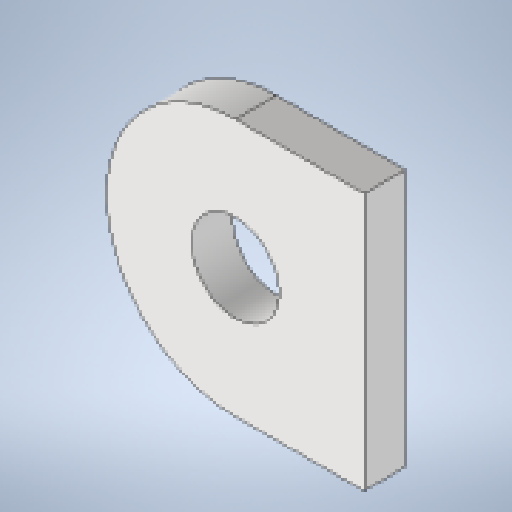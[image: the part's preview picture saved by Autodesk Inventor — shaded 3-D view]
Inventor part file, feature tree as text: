
AUTODESK INVENTOR PART (.ipt)
format: ipt  version: 2025.1 (Build 291241020, 241B)  size: 160,768 bytes
history: native  units: mm
features: other x2, sheet_metal_op x1, sketch x1
ambient origin geometry x8: Origin, YZ Plane, XZ Plane, XY Plane, X Axis, Y Axis, Z Axis, Center Point
bodies: Solid1 (feature_tree)
feature tree (4):
  sheet_metal_op  "Face1"
  sketch  "Sketch1"  dims[d0=50.0mm d1=50.0mm d2=8.0mm d14=17.0mm]
  other  "Plate1"
  other  "Definition1"
